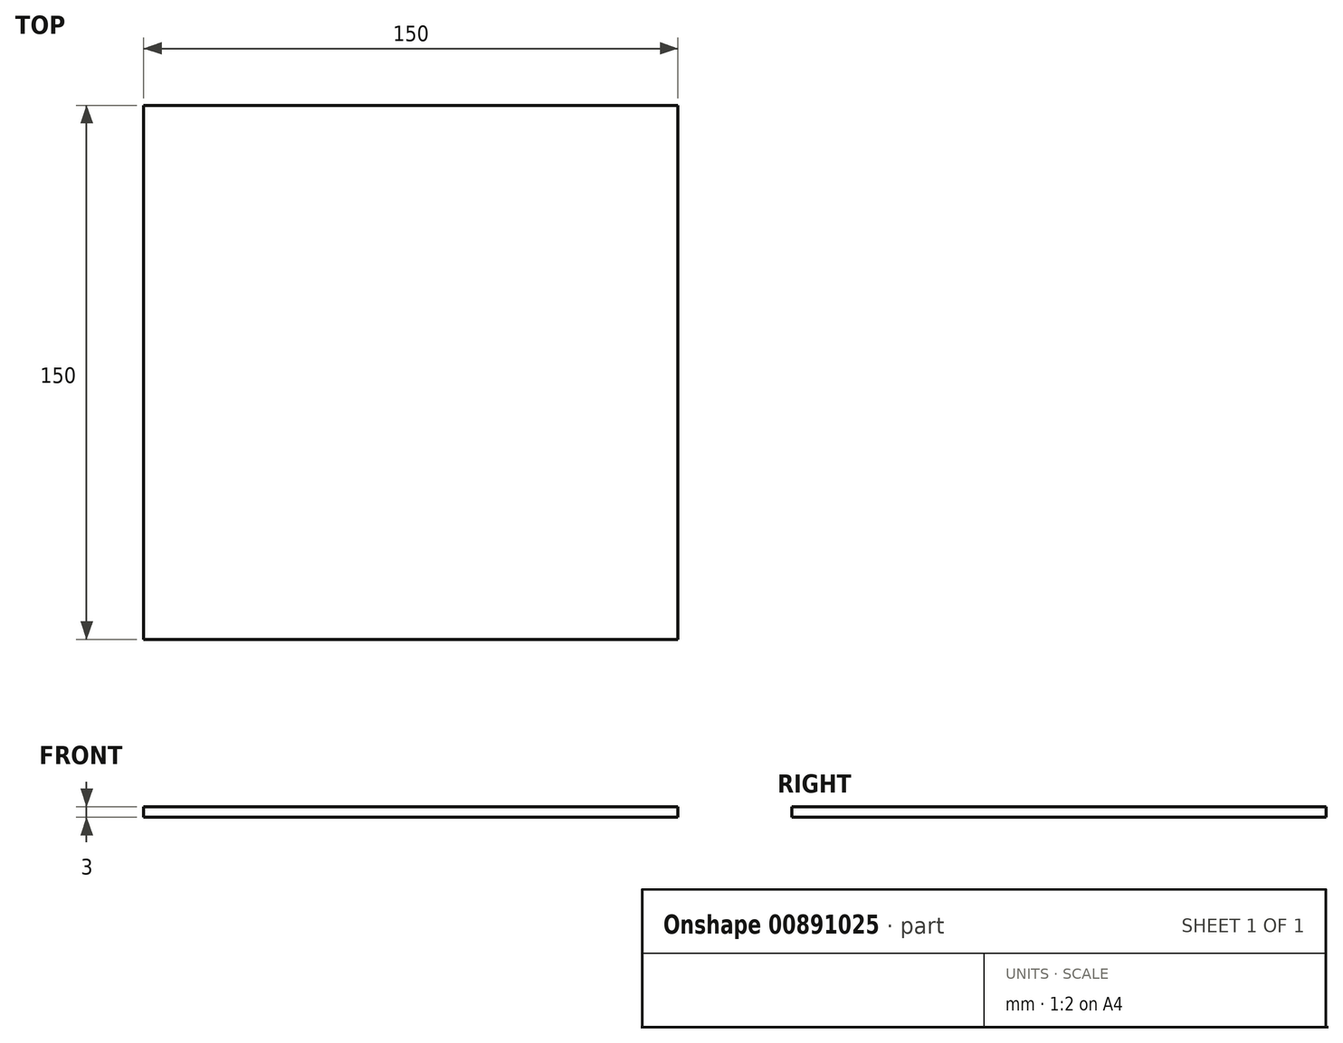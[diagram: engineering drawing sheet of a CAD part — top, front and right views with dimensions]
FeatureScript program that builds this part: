
annotation { "Feature Type Name" : "Feature", "Feature Type Description" : "" }
export const myFeature = defineFeature(function(context is Context, id is Id, definition is map)
    precondition{}
    {
        {
            var Q0;
            Q0=qCreatedBy(makeId("Top.planeOp"),FACE);
            var sketch = newSketch(context, id + "F0", { "sketchPlane" : qUnion([Q0])});
            skLineSegment(sketch, "E0.bottom", {"start": v(-75, 75) * mm, "end": v(75, 75) * mm});
            skLineSegment(sketch, "E0.top", {"start": v(-75, -75) * mm, "end": v(75, -75) * mm});
            skLineSegment(sketch, "E0.left", {"start": v(-75, 75) * mm, "end": v(-75, -75) * mm});
            skLineSegment(sketch, "E0.right", {"start": v(75, 75) * mm, "end": v(75, -75) * mm});
            skPoint(sketch, "E0.middle", {"position": v(0, 0) * mm});
            skSolve(sketch);
        }
        {
            var Q0;
            Q0=makeQuery(id+"F0.imprint","IMPRINT",FACE,{"disambiguationData":[TD([[makeQuery(id+"F0.imprint","IMPRINT",EDGE,{"derivedFrom":sQuery(id+"F0.wireOp",EDGE,"E0.bottom")}),-1.0]])]});
            extrude(context, id + "F1", {"entities" : qUnion([Q0]), "depth" : 3 * mm, "offsetDistance" : 25 * mm});
        }
    });
